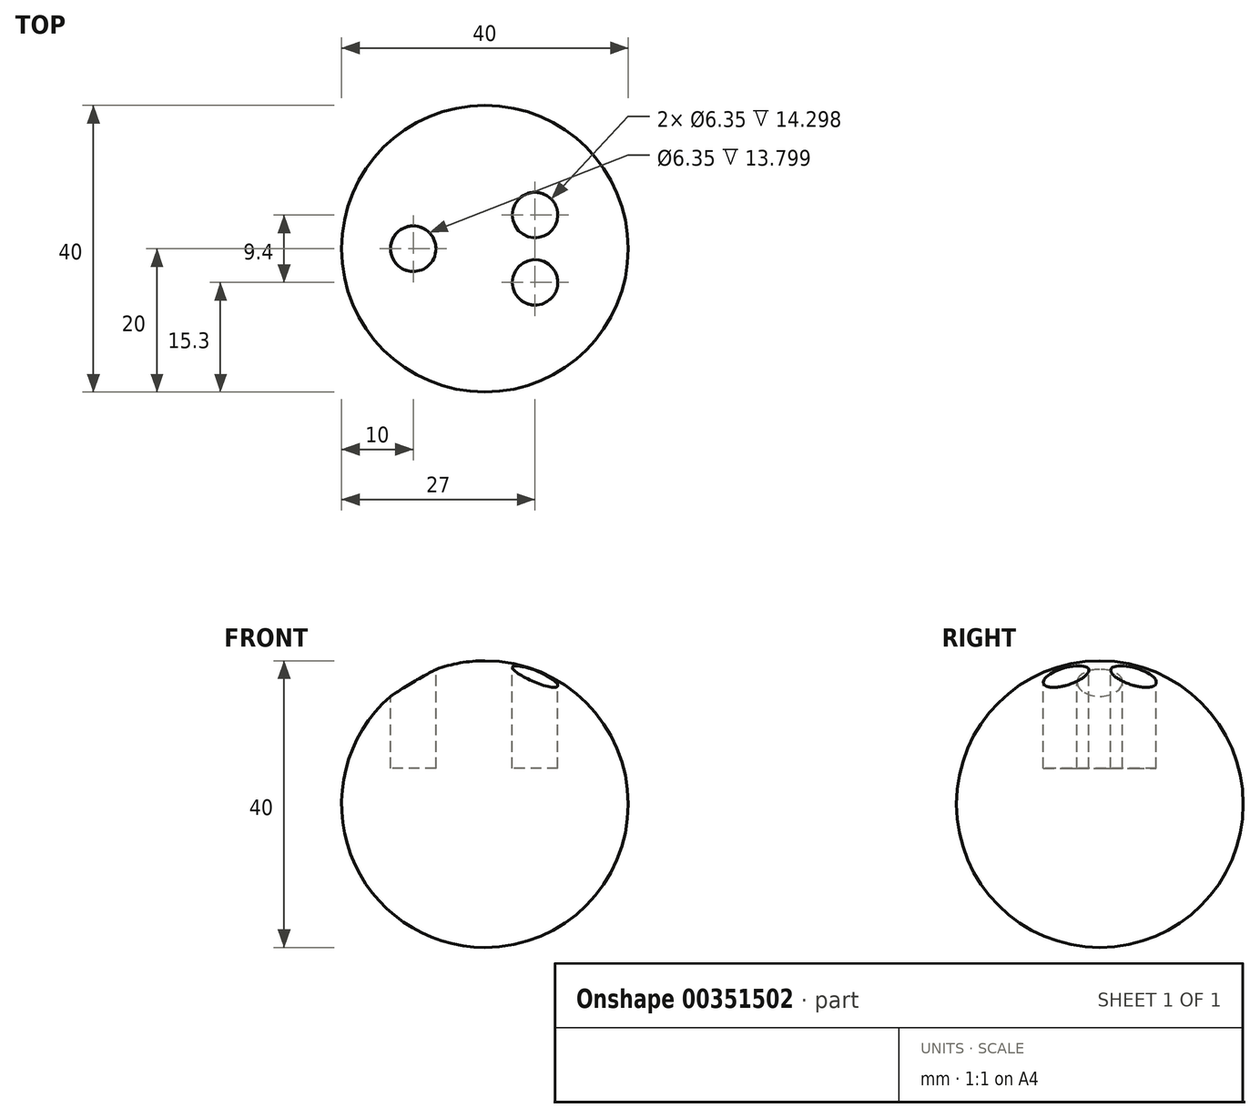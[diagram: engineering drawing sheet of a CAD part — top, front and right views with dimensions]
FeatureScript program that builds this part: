
annotation { "Feature Type Name" : "Feature", "Feature Type Description" : "" }
export const myFeature = defineFeature(function(context is Context, id is Id, definition is map)
    precondition{}
    {
        {
            var Q0;
            Q0=qCreatedBy(makeId("Front.planeOp"),FACE);
            var sketch = newSketch(context, id + "F0", { "sketchPlane" : qUnion([Q0])});
            skArc(sketch, "E0", {"start": v(0, -40) * mm, "mid": v(20, -20) * mm, "end": v(0, 0) * mm});
            skLineSegment(sketch, "E1", {"start": v(0, 0) * mm, "end": v(0, -40) * mm});
            skSolve(sketch);
        }
        {
            var Q0;
            Q0 = qSketchRegion(id + "F0", true);
            var Q1;
            Q1=sQuery(id+"F0.wireOp",EDGE,"E1");
            revolve(context, id + "F1", {"entities" : qUnion([Q0]), "axis" : qUnion([Q1]), "revolveType" : RevolveType.FULL});
        }
        {
            var Q0;
            Q0=qCreatedBy(makeId("Top.planeOp"),FACE);
            var sketch = newSketch(context, id + "F2", { "sketchPlane" : qUnion([Q0])});
            skCircle(sketch, "E2", {"center": v(-10, 0) * mm, "radius": 3.18 * mm});
            skCircle(sketch, "E3", {"center": v(7, 4.7) * mm, "radius": 3.17 * mm});
            skCircle(sketch, "E4", {"center": v(7, -4.7) * mm, "radius": 3.17 * mm});
            skSolve(sketch);
        }
        {
            var Q0;
            Q0 = qSketchRegion(id + "F2", true);
            extrude(context, id + "F3", {"entities" : qUnion([Q0]), "operationType" : NewBodyOperationType.REMOVE, "oppositeDirection" : true, "depth" : 15 * mm});
        }
    });
